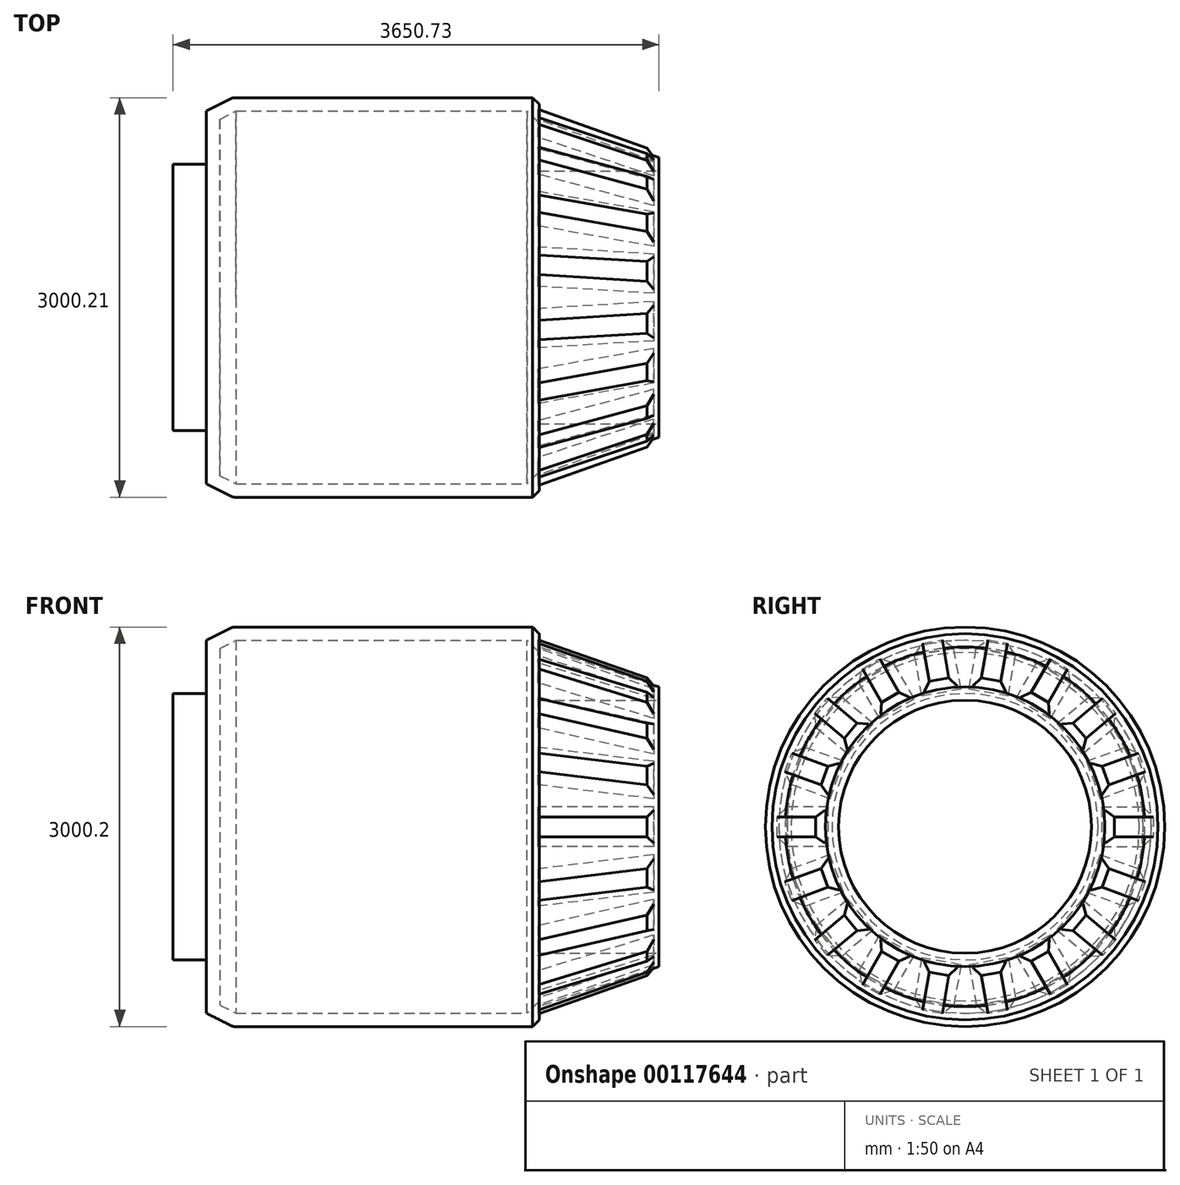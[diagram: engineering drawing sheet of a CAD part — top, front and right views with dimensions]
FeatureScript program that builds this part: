
annotation { "Feature Type Name" : "Feature", "Feature Type Description" : "" }
export const myFeature = defineFeature(function(context is Context, id is Id, definition is map)
    precondition{}
    {
        {
            var Q0;
            Q0=qCreatedBy(makeId("Top.planeOp"),FACE);
            var sketch = newSketch(context, id + "F0", { "sketchPlane" : qUnion([Q0])});
            skLineSegment(sketch, "E0.bottom", {"start": v(-1251.1, 1499.9) * mm, "end": v(1250.06, 1500) * mm});
            skPoint(sketch, "E0.middle", {"position": v(0, 0) * mm});
            skLineSegment(sketch, "E1", {"start": v(2149.64, 950) * mm, "end": v(1249.64, 950) * mm});
            skLineSegment(sketch, "E2", {"start": v(1250.06, 1500) * mm, "end": v(1248.9, -0.1) * mm});
            skLineSegment(sketch, "E3", {"start": v(1248.9, -0.1) * mm, "end": v(-1251.1, -0.1) * mm});
            skLineSegment(sketch, "E4", {"start": v(-1251.1, 1499.9) * mm, "end": v(-1251.1, -0.1) * mm});
            skLineSegment(sketch, "E5", {"start": v(2149.64, 950) * mm, "end": v(2149.64, 1050) * mm});
            skLineSegment(sketch, "E6", {"start": v(1250, 1350) * mm, "end": v(2149.64, 1050) * mm});
            skLineSegment(sketch, "E7", {"start": v(1250, 1350) * mm, "end": v(1249.64, 950) * mm});
            skSolve(sketch);
        }
        {
            var Q0;
            {var subQ3=sQuery(id+"F0.wireOp",EDGE,"E0.bottom");Q0=makeQuery(id+"F0.imprint","IMPRINT",FACE,{"disambiguationData":[TD([[makeQuery(id+"F0.imprint","IMPRINT",EDGE,{"derivedFrom":subQ3}),-1.0]])]});}
            var sketch = newSketch(context, id + "F1", { "sketchPlane" : qUnion([Q0])});
            skLineSegment(sketch, "E8", {"start": v(2110.5, 1104.83) * mm, "end": v(2110.5, 1025.87) * mm});
            skLineSegment(sketch, "E9", {"start": v(2110.5, 1025.87) * mm, "end": v(1241.62, 1333.62) * mm});
            skLineSegment(sketch, "E10", {"start": v(1241.62, 1333.62) * mm, "end": v(1241.62, 1412.58) * mm});
            skLineSegment(sketch, "E11", {"start": v(2110.5, 1104.83) * mm, "end": v(1241.62, 1412.58) * mm});
            skSolve(sketch);
        }
        {
            var Q0;
            {var subQ0=sQuery(id+"F0.wireOp",EDGE,"8c3RHRXC-WC5Y-towL-4QDg-a1nwEATf3NPt");Q0=makeQuery(id+"F0.imprint","IMPRINT",FACE,{"disambiguationData":[TD([[makeQuery(id+"F0.imprint","IMPRINT",EDGE,{"derivedFrom":subQ0}),-1.0]])]});}
            var Q1;
            {var subQ4=sQuery(id+"F0.wireOp",EDGE,"E0.bottom");Q1=makeQuery(id+"F0.imprint","IMPRINT",FACE,{"disambiguationData":[TD([[makeQuery(id+"F0.imprint","IMPRINT",EDGE,{"derivedFrom":subQ4}),-1.0]])]});}
            var Q2;
            Q2=sQuery(id+"F0.wireOp",EDGE,"E3");
            revolve(context, id + "F2", {"entities" : qUnion([Q0, Q1]), "axis" : qUnion([Q2]), "revolveType" : RevolveType.FULL});
        }
        {
            var Q0;
            {var subQ3=sQuery(id+"F0.wireOp",EDGE,"E1");Q0=makeQuery(id+"F0.imprint","IMPRINT",FACE,{"disambiguationData":[TD([[makeQuery(id+"F0.imprint","IMPRINT",EDGE,{"derivedFrom":subQ3}),-1.0]])]});}
            var Q1;
            Q1=sQuery(id+"F0.wireOp",EDGE,"E3");
            revolve(context, id + "F3", {"entities" : qUnion([Q0]), "axis" : qUnion([Q1]), "revolveType" : RevolveType.FULL});
        }
        {
            var Q0;
            Q0=makeQuery(id+"F2.opRevolve","SWEPT_EDGE",EDGE,{"disambiguationData":[OSD([sQuery(id+"F0.wireOp",EDGE,"E0.bottom"),sQuery(id+"F0.wireOp",EDGE,"E4")])]});
            chamfer(context, id + "F4", {"entities" : qUnion([Q0]), "chamferType" : ChamferType.TWO_OFFSETS, "width1" : 200 * mm, "oppositeDirection" : false, "width2" : 100 * mm, "tangentPropagation" : true});
        }
        {
            var Q0;
            {var subQ0=sQuery(id+"F0.wireOp",EDGE,"E0.bottom");Q0=makeQuery(id+"F4.opChamfer","BLEND_EDGE",EDGE,{"blendedFrom":[makeQuery(id+"F2.opRevolve","SWEPT_EDGE",EDGE,{"disambiguationData":[OSD([subQ0,sQuery(id+"F0.wireOp",EDGE,"E4")])]}),makeQuery(id+"F2.opRevolve","SWEPT_FACE",FACE,{"disambiguationData":[OSD([subQ0])]})],"blendedInto":[makeQuery(id+"F2.opRevolve","SWEPT_FACE",FACE,{"disambiguationData":[OSD([subQ0])]})]});}
            fillet(context, id + "F5", {"entities" : qUnion([Q0]), "radius" : 50 * mm, "tangentPropagation" : true, "allowEdgeOverflow" : false});
        }
        {
            var Q0;
            Q0=makeQuery(id+"F2.opRevolve","SWEPT_EDGE",EDGE,{"disambiguationData":[OSD([sQuery(id+"F0.wireOp",EDGE,"E0.bottom"),sQuery(id+"F0.wireOp",EDGE,"E2")])]});
            chamfer(context, id + "F6", {"entities" : qUnion([Q0]), "width" : 50 * mm, "tangentPropagation" : true});
        }
        {
            var Q0;
            {var subQ0=sQuery(id+"F0.wireOp",EDGE,"E2");Q0=makeQuery(id+"F2.opRevolve","SWEPT_FACE",FACE,{"disambiguationData":[OSD([subQ0]),TDD([makeQuery(id+"F0.imprint","IMPRINT",EDGE,{"disambiguationData":[TD([[makeQuery(id+"F0.imprint","INTERSECT",VERTEX,{"derivedFrom":[sQuery(id+"F0.wireOp",EDGE,"E1"),subQ0]}),-1.0]])],"derivedFrom":subQ0})])]});}
            shell(context, id + "F7", {"entities" : qUnion([Q0]), "thickness" : 100 * mm});
        }
        {
            var Q0;
            Q0 = qSketchRegion(id + "F1", true);
            extrude(context, id + "F8", {"entities" : qUnion([Q0]), "depth" : 300 * mm, "symmetric" : true});
        }
        {
            var Q0;
            Q0=makeQuery(id+"F8.opExtrude","CAP_EDGE",EDGE,{"disambiguationData":[OSD([sQuery(id+"F1.wireOp",EDGE,"E11")])],"isStart":false});
            var Q1;
            Q1=makeQuery(id+"F8.opExtrude","SWEPT_EDGE",EDGE,{"disambiguationData":[OSD([sQuery(id+"F1.wireOp",EDGE,"E8"),sQuery(id+"F1.wireOp",EDGE,"E11")])]});
            var Q2;
            Q2=makeQuery(id+"F8.opExtrude","CAP_EDGE",EDGE,{"disambiguationData":[OSD([sQuery(id+"F1.wireOp",EDGE,"E11")])],"isStart":true});
            chamfer(context, id + "F9", {"entities" : qUnion([Q0, Q1, Q2]), "chamferType" : ChamferType.OFFSET_ANGLE, "width" : 75 * mm, "oppositeDirection" : false, "angle" : 45 * degree, "tangentPropagation" : true});
        }
        {
            var Q0;
            Q0=makeQuery(id+"F8.opExtrude","SWEPT_BODY",BODY,{"disambiguationData":[OSD([sQuery(id+"F1.wireOp",EDGE,"E8"),sQuery(id+"F1.wireOp",EDGE,"E9"),sQuery(id+"F1.wireOp",EDGE,"E10"),sQuery(id+"F1.wireOp",EDGE,"E11")])]});
            var Q1;
            Q1=makeQuery(id+"F3.opRevolve","SWEPT_FACE",FACE,{"disambiguationData":[OSD([sQuery(id+"F0.wireOp",EDGE,"E6")])]});
            circularPattern(context, id + "F10", {"entities" : qUnion([Q0]), "axis" : qUnion([Q1]), "angle" : 20 * degree, "instanceCount" : 18});
        }
        {
            var Q0;
            Q0=makeQuery(id+"F2.opRevolve","SWEPT_FACE",FACE,{"disambiguationData":[OSD([sQuery(id+"F0.wireOp",EDGE,"E4")])]});
            var sketch = newSketch(context, id + "F11", { "sketchPlane" : qUnion([Q0])});
            skCircle(sketch, "E12", {"center": v(0, 0) * mm, "radius": 1000 * mm});
            skSolve(sketch);
        }
        {
            var Q0;
            Q0=makeQuery(id+"F11.imprint","IMPRINT",FACE,{"disambiguationData":[TD([[makeQuery(id+"F11.imprint","IMPRINT",EDGE,{"derivedFrom":sQuery(id+"F11.wireOp",EDGE,"E12")}),1.0]])]});
            extrude(context, id + "F12", {"entities" : qUnion([Q0]), "operationType" : NewBodyOperationType.ADD, "depth" : 250 * mm});
        }
    });
